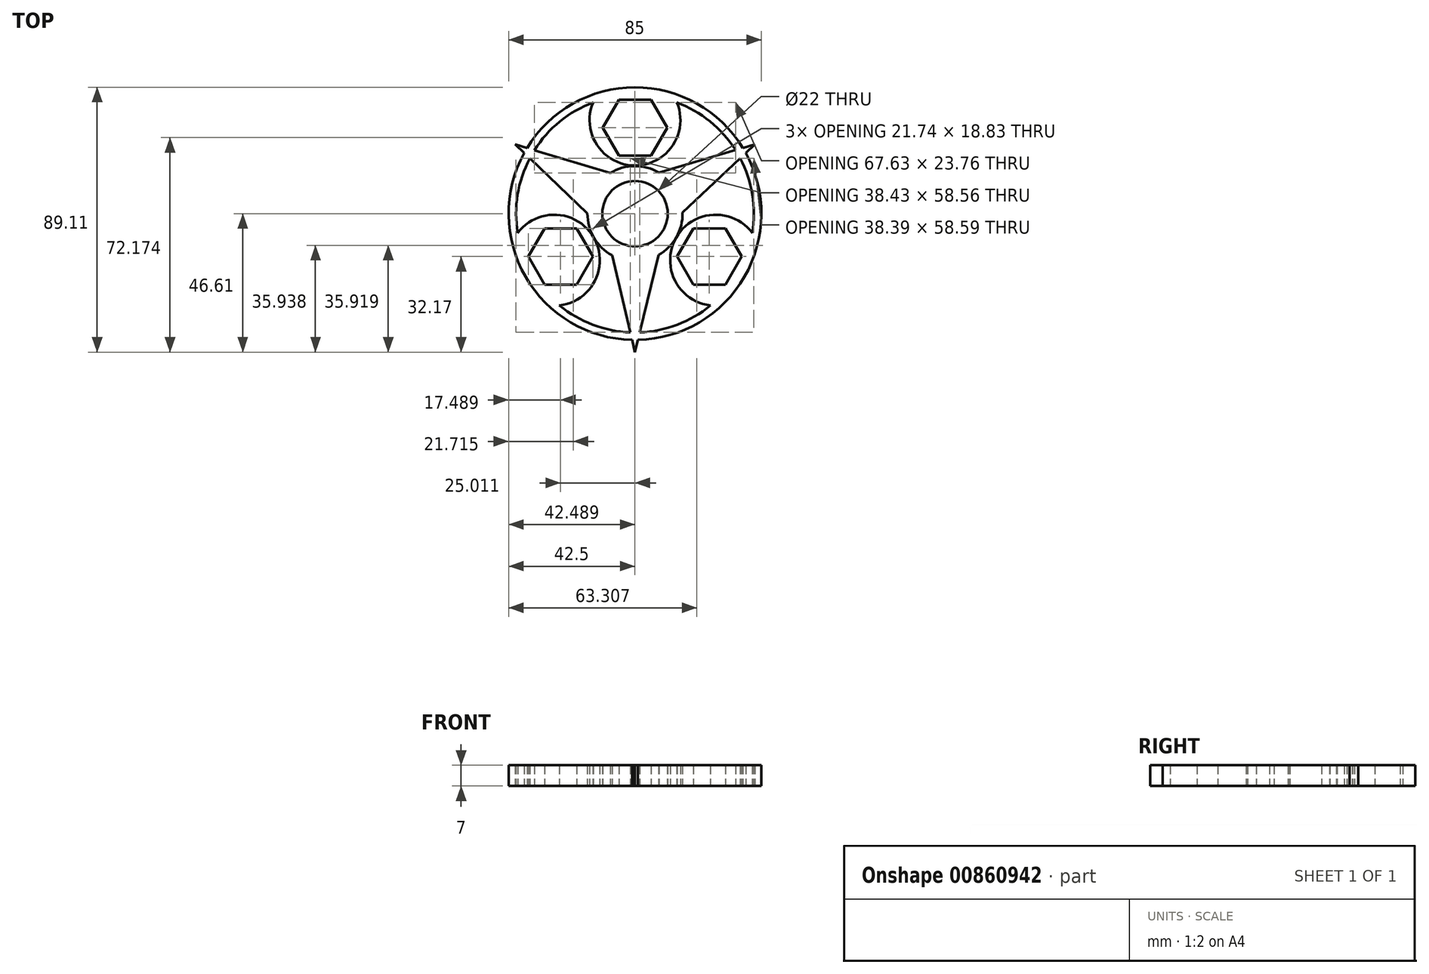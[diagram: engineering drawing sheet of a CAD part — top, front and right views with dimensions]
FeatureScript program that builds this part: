
annotation { "Feature Type Name" : "Feature", "Feature Type Description" : "" }
export const myFeature = defineFeature(function(context is Context, id is Id, definition is map)
    precondition{}
    {
        {
            var Q0;
            Q0=qCreatedBy(makeId("Top.planeOp"),FACE);
            var sketch = newSketch(context, id + "F0", { "sketchPlane" : qUnion([Q0])});
            skCircle(sketch, "E0", {"center": v(0, 0) * mm, "radius": 11 * mm});
            skArc(sketch, "E1.0", {"start": v(8.05, 13.83) * mm, "mid": v(-0.14, 16) * mm, "end": v(-8.3, 13.68) * mm});
            skArc(sketch, "E2", {"start": v(-14.07, 37.44) * mm, "mid": v(-25.27, 31) * mm, "end": v(-33.83, 21.34) * mm});
            skLineSegment(sketch, "E3", {"start": v(-7.7, -14.02) * mm, "end": v(0, -46.61) * mm});
            skLineSegment(sketch, "E4", {"start": v(0, -46.61) * mm, "end": v(7.95, -13.89) * mm});
            skLineSegment(sketch, "E5.1.0", {"start": v(16, 0.34) * mm, "end": v(40.37, 23.3) * mm});
            skLineSegment(sketch, "E5.1.1", {"start": v(40.37, 23.3) * mm, "end": v(8.05, 13.83) * mm});
            skLineSegment(sketch, "E5.2.0", {"start": v(-8.3, 13.68) * mm, "end": v(-40.37, 23.3) * mm});
            skLineSegment(sketch, "E5.2.1", {"start": v(-40.37, 23.3) * mm, "end": v(-16, 0.06) * mm});
            skArc(sketch, "E6", {"start": v(-37.3, 20.38) * mm, "mid": v(-36.8, -21.26) * mm, "end": v(-0.98, -42.49) * mm});
            skArc(sketch, "E7", {"start": v(-14.07, 37.44) * mm, "mid": v(0, 16.2) * mm, "end": v(14.07, 37.44) * mm});
            skArc(sketch, "E8.trimOffspring", {"start": v(-35.42, 18.59) * mm, "mid": v(-39.5, 6.36) * mm, "end": v(-39.46, -6.53) * mm});
            skArc(sketch, "E9.trimOffspring", {"start": v(1.61, -39.97) * mm, "mid": v(14.24, -37.38) * mm, "end": v(25.39, -30.9) * mm});
            skArc(sketch, "E10.trimOffspring", {"start": v(1, -42.49) * mm, "mid": v(36.81, -21.24) * mm, "end": v(37.28, 20.4) * mm});
            skArc(sketch, "E11.trimOffspring", {"start": v(39.46, -6.53) * mm, "mid": v(39.49, 6.38) * mm, "end": v(35.4, 18.62) * mm});
            skArc(sketch, "E12.trimOffspring", {"start": v(-25.39, -30.9) * mm, "mid": v(-14.22, -37.39) * mm, "end": v(-1.57, -39.97) * mm});
            skArc(sketch, "E13.trimOffspring", {"start": v(33.8, 21.38) * mm, "mid": v(25.25, 31.02) * mm, "end": v(14.07, 37.44) * mm});
            skArc(sketch, "E14.trimOffspring", {"start": v(36.3, 22.11) * mm, "mid": v(-0.01, 42.5) * mm, "end": v(-36.3, 22.09) * mm});
            skArc(sketch, "E15.trimOffspring", {"start": v(7.95, -13.89) * mm, "mid": v(13.93, -7.88) * mm, "end": v(16, 0.34) * mm});
            skArc(sketch, "E16.trimOffspring", {"start": v(-16, 0.06) * mm, "mid": v(-13.79, -8.12) * mm, "end": v(-7.7, -14.02) * mm});
            skArc(sketch, "E17.1.1", {"start": v(-25.39, -30.9) * mm, "mid": v(-13.88, -8.02) * mm, "end": v(-39.46, -6.53) * mm});
            skArc(sketch, "E17.2.1", {"start": v(39.46, -6.53) * mm, "mid": v(13.88, -8.02) * mm, "end": v(25.39, -30.9) * mm});
            skLineSegment(sketch, "E18.0", {"start": v(-5.44, 38.3) * mm, "end": v(5.44, 38.3) * mm});
            skLineSegment(sketch, "E18.1", {"start": v(5.44, 38.3) * mm, "end": v(10.87, 28.88) * mm});
            skLineSegment(sketch, "E18.2", {"start": v(10.87, 28.88) * mm, "end": v(5.44, 19.47) * mm});
            skLineSegment(sketch, "E18.3", {"start": v(5.44, 19.47) * mm, "end": v(-5.44, 19.47) * mm});
            skLineSegment(sketch, "E18.4", {"start": v(-5.44, 19.47) * mm, "end": v(-10.87, 28.88) * mm});
            skLineSegment(sketch, "E18.5", {"start": v(-10.87, 28.88) * mm, "end": v(-5.44, 38.3) * mm});
            skPoint(sketch, "E18.0.midPoint", {"position": v(0, 38.3) * mm});
            skLineSegment(sketch, "E19.1.0", {"start": v(-19.58, -23.86) * mm, "end": v(-30.45, -23.86) * mm});
            skLineSegment(sketch, "E19.1.1", {"start": v(-30.45, -23.86) * mm, "end": v(-35.88, -14.44) * mm});
            skLineSegment(sketch, "E19.1.2", {"start": v(-35.88, -14.44) * mm, "end": v(-30.45, -5.03) * mm});
            skLineSegment(sketch, "E19.1.3", {"start": v(-30.45, -5.03) * mm, "end": v(-19.58, -5.03) * mm});
            skLineSegment(sketch, "E19.1.4", {"start": v(-19.58, -5.03) * mm, "end": v(-14.14, -14.44) * mm});
            skLineSegment(sketch, "E19.1.5", {"start": v(-14.14, -14.44) * mm, "end": v(-19.58, -23.86) * mm});
            skLineSegment(sketch, "E19.2.0", {"start": v(30.45, -5.03) * mm, "end": v(35.88, -14.44) * mm});
            skLineSegment(sketch, "E19.2.1", {"start": v(35.88, -14.44) * mm, "end": v(30.45, -23.86) * mm});
            skLineSegment(sketch, "E19.2.2", {"start": v(30.45, -23.86) * mm, "end": v(19.58, -23.86) * mm});
            skLineSegment(sketch, "E19.2.3", {"start": v(19.58, -23.86) * mm, "end": v(14.14, -14.44) * mm});
            skLineSegment(sketch, "E19.2.4", {"start": v(14.14, -14.44) * mm, "end": v(19.58, -5.03) * mm});
            skLineSegment(sketch, "E19.2.5", {"start": v(19.58, -5.03) * mm, "end": v(30.45, -5.03) * mm});
            skSolve(sketch);
        }
        {
            var Q0;
            Q0 = qSketchRegion(id + "F0", true);
            extrude(context, id + "F1", {"entities" : qUnion([Q0]), "depth" : 7 * mm, "offsetDistance" : 25 * mm});
        }
    });
